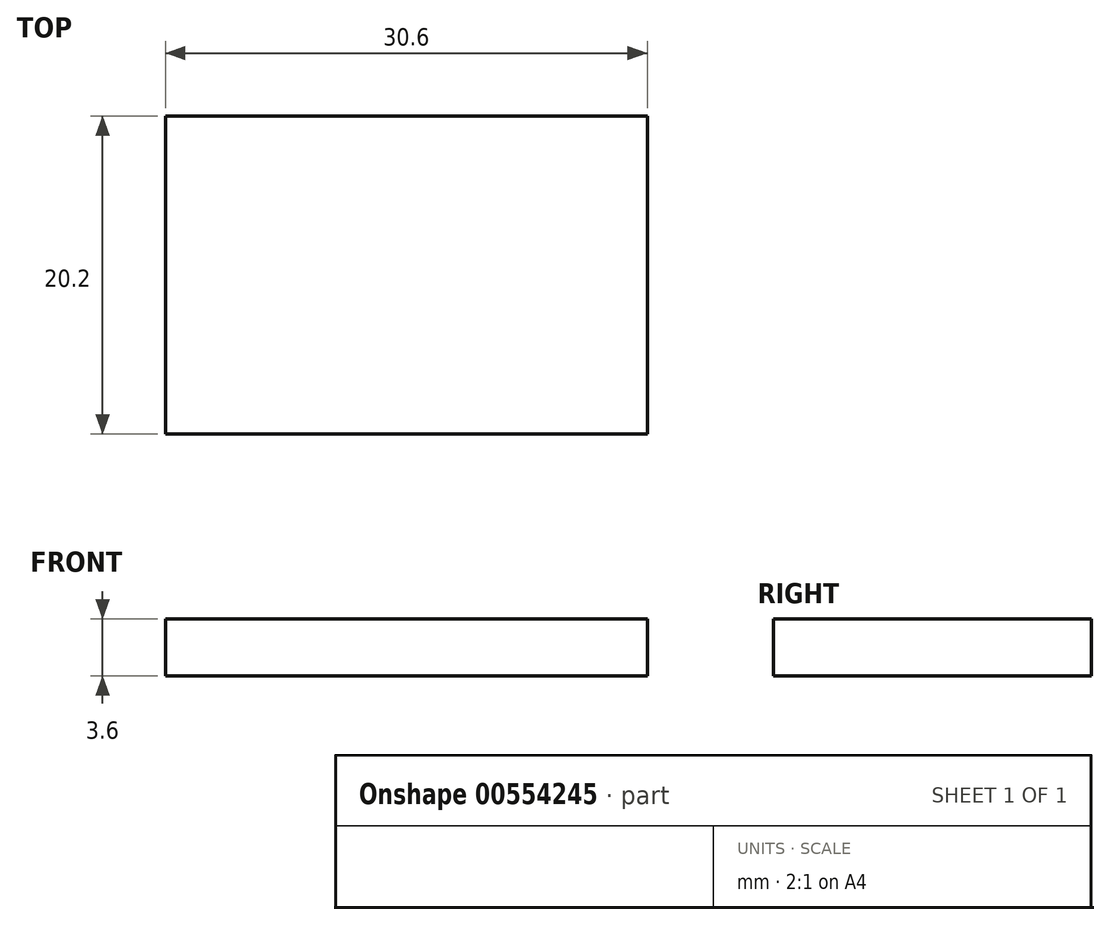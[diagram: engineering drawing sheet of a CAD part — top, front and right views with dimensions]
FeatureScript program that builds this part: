
annotation { "Feature Type Name" : "Feature", "Feature Type Description" : "" }
export const myFeature = defineFeature(function(context is Context, id is Id, definition is map)
    precondition{}
    {
        {
            var Q0;
            Q0=qCreatedBy(makeId("Top.planeOp"),FACE);
            var sketch = newSketch(context, id + "F0", { "sketchPlane" : qUnion([Q0])});
            skLineSegment(sketch, "E0.bottom", {"start": v(-14.45, 8.1) * mm, "end": v(16.15, 8.1) * mm});
            skLineSegment(sketch, "E0.top", {"start": v(-14.45, -12.1) * mm, "end": v(16.15, -12.1) * mm});
            skLineSegment(sketch, "E0.left", {"start": v(-14.45, 8.1) * mm, "end": v(-14.45, -12.1) * mm});
            skLineSegment(sketch, "E0.right", {"start": v(16.15, 8.1) * mm, "end": v(16.15, -12.1) * mm});
            skSolve(sketch);
        }
        {
            var Q0;
            Q0=makeQuery(id+"F0.imprint","IMPRINT",FACE,{"disambiguationData":[TD([[makeQuery(id+"F0.imprint","IMPRINT",EDGE,{"derivedFrom":sQuery(id+"F0.wireOp",EDGE,"E0.bottom")}),-1.0]])]});
            extrude(context, id + "F1", {"entities" : qUnion([Q0]), "depth" : 3.6 * mm});
        }
    });
